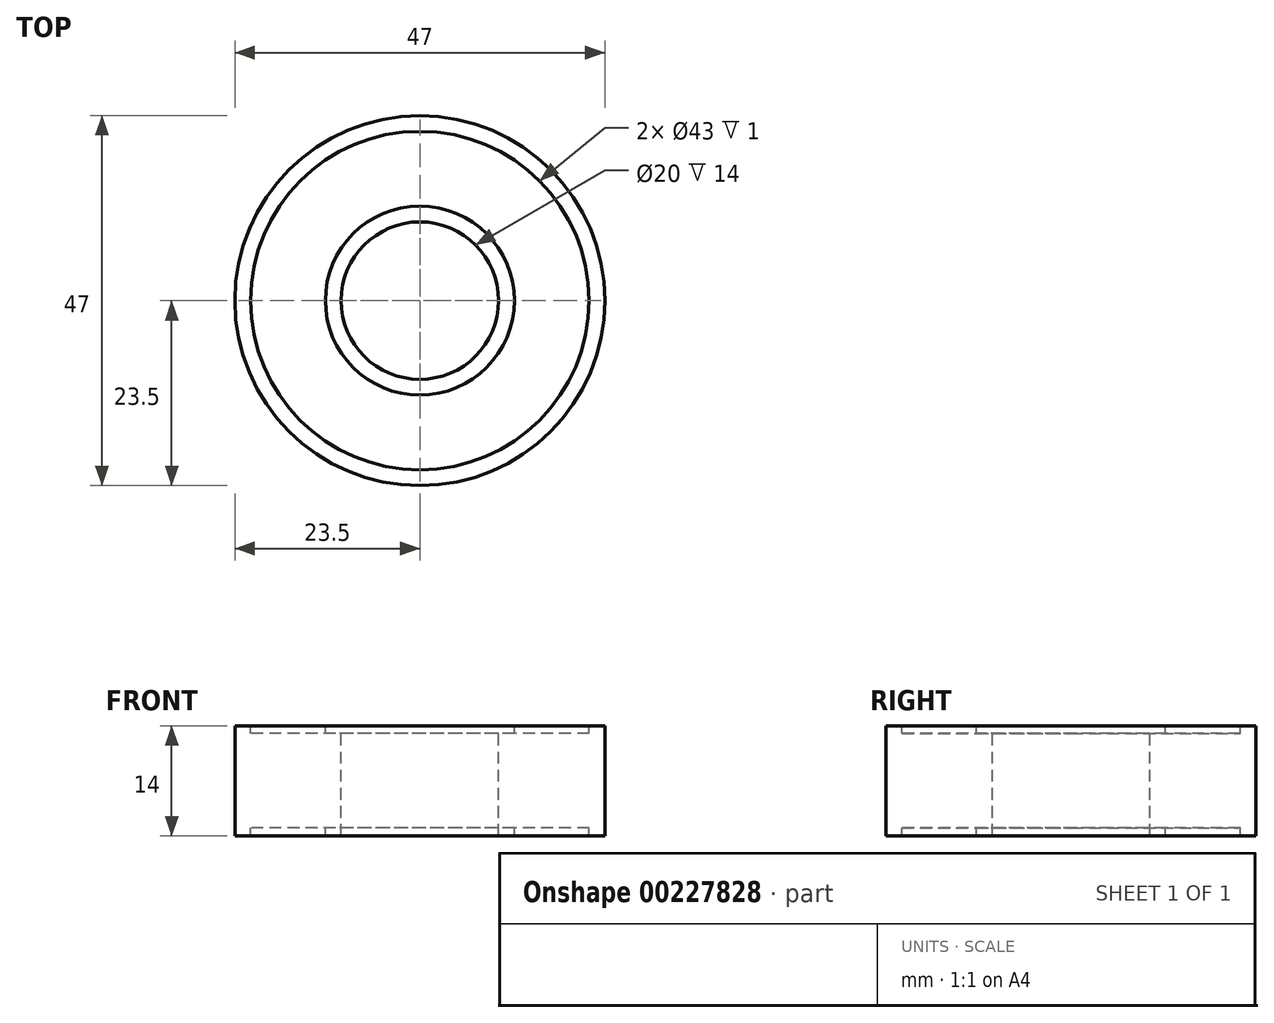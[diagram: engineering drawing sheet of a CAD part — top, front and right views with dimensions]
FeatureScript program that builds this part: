
annotation { "Feature Type Name" : "Feature", "Feature Type Description" : "" }
export const myFeature = defineFeature(function(context is Context, id is Id, definition is map)
    precondition{}
    {
        {
            var Q0;
            Q0=qCreatedBy(makeId("Front.planeOp"),FACE);
            var sketch = newSketch(context, id + "F0", { "sketchPlane" : qUnion([Q0])});
            skLineSegment(sketch, "E0.MirrorCS", {"start": v(-21.5, -6) * mm, "end": v(-12, -6) * mm});
            skLineSegment(sketch, "E1.MirrorCS", {"start": v(-21.5, -7) * mm, "end": v(-23.5, -7) * mm});
            skLineSegment(sketch, "E2.MirrorCS", {"start": v(-12, -7) * mm, "end": v(-12, -6) * mm});
            skLineSegment(sketch, "E3.MirrorCS", {"start": v(-21.5, -7) * mm, "end": v(-21.5, -6) * mm});
            skLineSegment(sketch, "E4.MirrorCS", {"start": v(-10, -7) * mm, "end": v(-12, -7) * mm});
            skLineSegment(sketch, "E5.MirrorCS", {"start": v(-21.5, 7) * mm, "end": v(-23.5, 7) * mm});
            skLineSegment(sketch, "E6.MirrorCS", {"start": v(-10, 7) * mm, "end": v(-12, 7) * mm});
            skLineSegment(sketch, "E7.MirrorCS", {"start": v(-21.5, 7) * mm, "end": v(-21.5, 6) * mm});
            skLineSegment(sketch, "E8.MirrorCS", {"start": v(-12, 7) * mm, "end": v(-12, 6) * mm});
            skLineSegment(sketch, "E9.MirrorCS", {"start": v(-21.5, 6) * mm, "end": v(-12, 6) * mm});
            skLineSegment(sketch, "E10", {"start": v(-10, -7) * mm, "end": v(-10, 0) * mm});
            skLineSegment(sketch, "E11", {"start": v(-23.5, -7) * mm, "end": v(-23.5, 0) * mm});
            skLineSegment(sketch, "E12.MirrorCS", {"start": v(-23.5, 7) * mm, "end": v(-23.5, 0) * mm});
            skLineSegment(sketch, "E13.MirrorCS", {"start": v(-10, 7) * mm, "end": v(-10, 0) * mm});
            skLineSegment(sketch, "E14", {"start": v(0, 9.56) * mm, "end": v(0, -9.15) * mm, "construction": true});
            skSolve(sketch);
        }
        {
            var Q0;
            Q0 = qSketchRegion(id + "F0", true);
            var Q1;
            Q1=sQuery(id+"F0.wireOp",EDGE,"E14");
            revolve(context, id + "F1", {"entities" : qUnion([Q0]), "axis" : qUnion([Q1]), "revolveType" : RevolveType.FULL});
        }
    });
